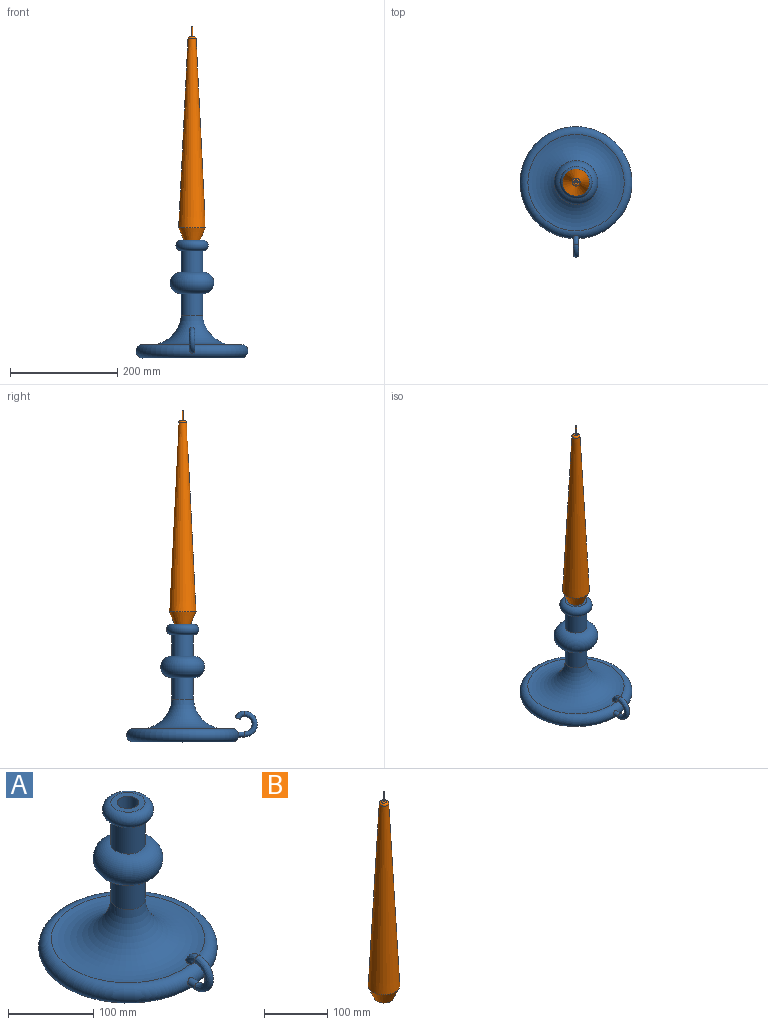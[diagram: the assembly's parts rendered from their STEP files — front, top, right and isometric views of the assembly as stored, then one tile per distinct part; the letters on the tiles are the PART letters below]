
ASSEMBLY  parts=2 mates=1
PART A: 14 faces, bbox 265.1x272.2x220.2 mm
  f0: plane 180x180mm, normal (0,0,-1), area 25446.9mm2, adj f1
  f1: torus R=92.17mm, axis (0,0,-1), area 27119.8mm2, adj f0,f2,f12
  f2: torus R=79.88mm, axis (0,0,-1), area 29640.4mm2, adj f1,f3
  f3: cylinder r=20mm len=40.04mm, axis (0,0,-1), area 5032mm2, adj f2,f4
  f4: torus R=20.93mm, axis (0,0,-1), area 13530.5mm2, adj f3,f5
  f5: cylinder r=20mm len=40mm, axis (0,0,-1), area 5026.5mm2, adj f4,f6
  f6: torus R=20mm, axis (0,0,-1), area 5204.5mm2, adj f5,f7
  f7: plane 40x40mm, normal (0,0,1), area 765.8mm2, adj f6,f8
  f8: cylinder r=12.5mm len=25mm, axis (0,0,1), area 1963.5mm2, adj f7,f9
  f9: plane 25x25mm, normal (0,0,1), area 490.9mm2, adj f8
  f10: plane 10x9.68mm, normal (0,0.25,-0.97), area 78.5mm2, adj f11
  f11: bspline ~20x18.24mm, area 521.4mm2, adj f10,f13
  f12: cylinder r=5mm len=12.78mm, axis (0,-1,0), area 361.3mm2, adj f1,f13
  f13: bspline ~48.34x24.56mm, area 1891.9mm2, adj f11,f12
PART B: 7 faces, bbox 50x50x400 mm
  f0: plane 30x30mm, normal (0,0,-1), area 706.9mm2, adj f1
  f1: cone r=15mm half-angle=23.6deg, axis (0,0,1), area 3141.6mm2, adj f0,f2
  f2: cone r=7.5mm half-angle=2.8deg, axis (0,0,-1), area 36146.1mm2, adj f1,f3
  f3: torus R=4mm, axis (0,0,-1), area 215.1mm2, adj f2,f4
  f4: plane 8x8mm, normal (0,0,1), area 47.1mm2, adj f3,f5
  f5: cylinder r=1mm len=20mm, axis (0,0,-1), area 125.7mm2, adj f4,f6
  f6: plane 2x2mm, normal (0,0,1), area 3.1mm2, adj f5
PLACE A t=(42.79,71.47,-15.14)mm
PLACE B t=(29.58,71.47,255.16)mm
MATE fastened B.f1 <-> A.f8  axis (0,0,-1) through (42.79,71.47,180.24)mm
